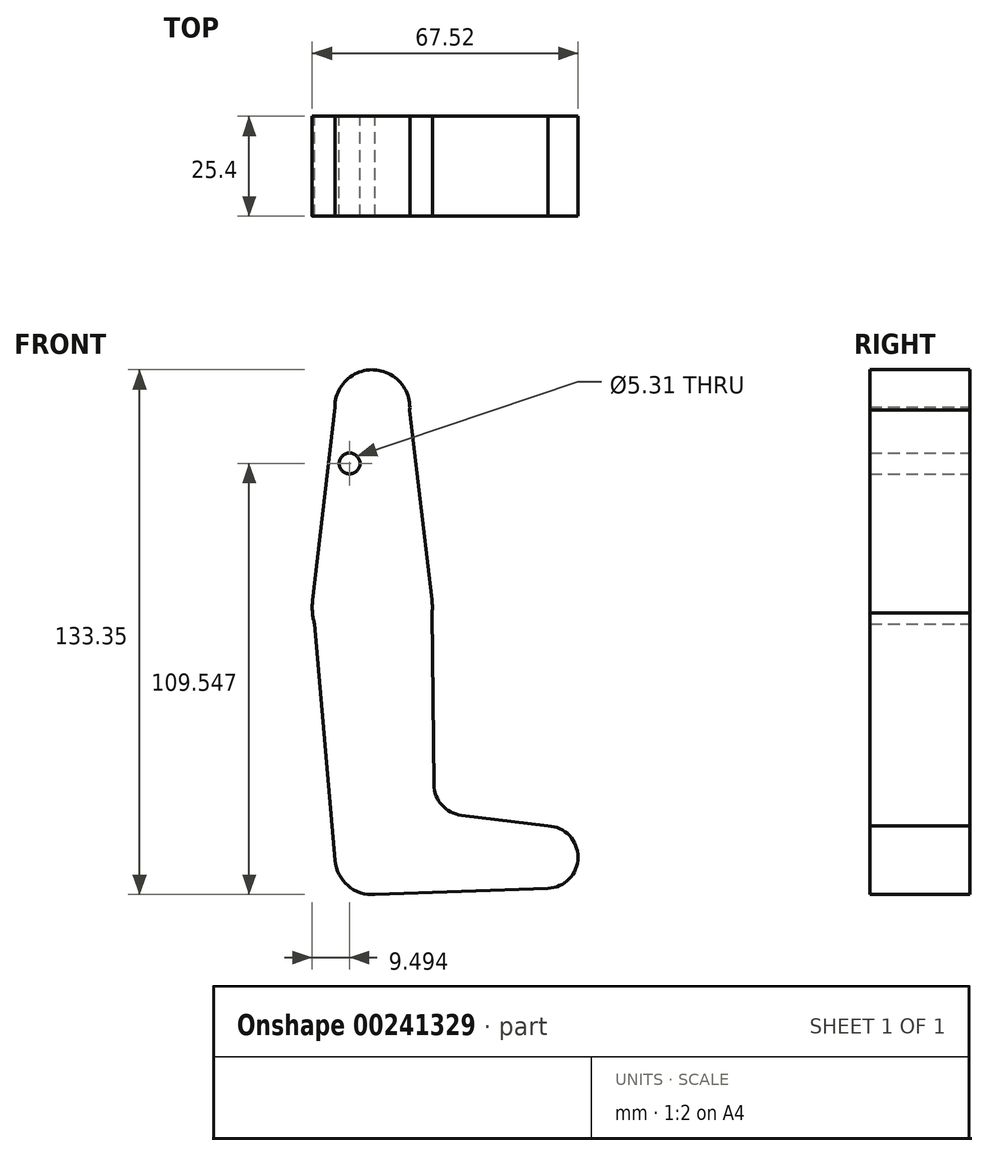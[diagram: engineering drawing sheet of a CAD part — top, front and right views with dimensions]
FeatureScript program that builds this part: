
annotation { "Feature Type Name" : "Feature", "Feature Type Description" : "" }
export const myFeature = defineFeature(function(context is Context, id is Id, definition is map)
    precondition{}
    {
        {
            var Q0;
            Q0=qCreatedBy(makeId("Front.planeOp"),FACE);
            var sketch = newSketch(context, id + "F0", { "sketchPlane" : qUnion([Q0])});
            skCircle(sketch, "E0", {"center": v(0, 45.6) * mm, "radius": 9.53 * mm});
            skCircle(sketch, "E1", {"center": v(0, -5.2) * mm, "radius": 15.26 * mm});
            skLineSegment(sketch, "E2", {"start": v(9.5, 44.83) * mm, "end": v(15.15, -3.43) * mm});
            skCircle(sketch, "E3", {"center": v(0, -68.7) * mm, "radius": 9.52 * mm});
            skLineSegment(sketch, "E4", {"start": v(-9.52, 45.66) * mm, "end": v(-15.16, -3.47) * mm});
            skLineSegment(sketch, "E5", {"start": v(-15.16, -3.47) * mm, "end": v(-9.5, -69.52) * mm});
            skLineSegment(sketch, "E6", {"start": v(0, -68.7) * mm, "end": v(44.32, -68.7) * mm});
            skCircle(sketch, "E7", {"center": v(44.32, -68.7) * mm, "radius": 7.94 * mm});
            skLineSegment(sketch, "E8", {"start": v(0, -78.23) * mm, "end": v(44.6, -76.64) * mm});
            skCircle(sketch, "E9", {"center": v(-5.77, 31.32) * mm, "radius": 2.65 * mm});
            skLineSegment(sketch, "E10", {"start": v(44.68, -60.78) * mm, "end": v(22.66, -58.09) * mm});
            skLineSegment(sketch, "E11", {"start": v(15.15, -3.43) * mm, "end": v(15.67, -50.28) * mm});
            skPoint(sketch, "E12.visualSharp", {"position": v(15.75, -57.24) * mm});
            skArc(sketch, "E12.filletArc", {"start": v(15.67, -50.28) * mm, "mid": v(17.7, -55.5) * mm, "end": v(22.66, -58.09) * mm});
            skSolve(sketch);
        }
        {
            var Q0;
            Q0 = qSketchRegion(id + "F0", true);
            extrude(context, id + "F1", {"entities" : qUnion([Q0]), "depth" : 25.4 * mm});
        }
    });
